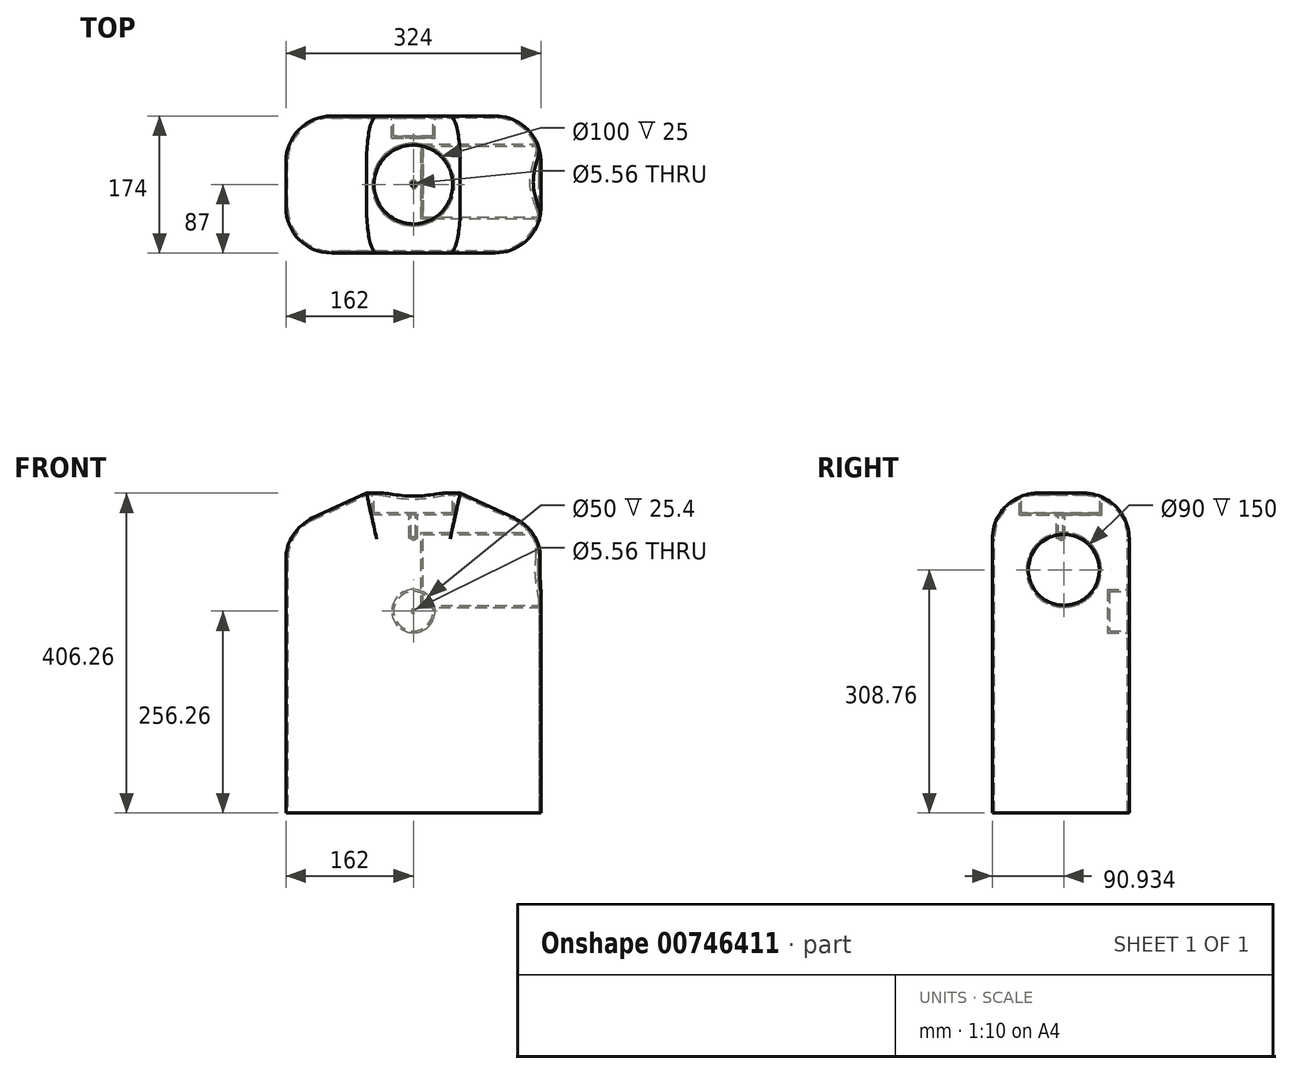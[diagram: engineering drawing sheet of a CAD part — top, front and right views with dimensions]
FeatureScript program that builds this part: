
annotation { "Feature Type Name" : "Feature", "Feature Type Description" : "" }
export const myFeature = defineFeature(function(context is Context, id is Id, definition is map)
    precondition{}
    {
        {
            var Q0;
            Q0=qCreatedBy(makeId("Front.planeOp"),FACE);
            var sketch = newSketch(context, id + "F0", { "sketchPlane" : qUnion([Q0])});
            skLineSegment(sketch, "E0.bottom", {"start": v(162, 203.13) * mm, "end": v(-162, 203.13) * mm});
            skLineSegment(sketch, "E0.top", {"start": v(162, -203.13) * mm, "end": v(-162, -203.13) * mm});
            skLineSegment(sketch, "E0.left", {"start": v(162, 203.13) * mm, "end": v(162, -203.13) * mm});
            skLineSegment(sketch, "E0.right", {"start": v(-162, 203.13) * mm, "end": v(-162, -203.13) * mm});
            skPoint(sketch, "E0.middle", {"position": v(0, 0) * mm});
            skSolve(sketch);
        }
        {
            var Q0;
            Q0=makeQuery(id+"F0.imprint","IMPRINT",FACE,{"disambiguationData":[TD([[makeQuery(id+"F0.imprint","IMPRINT",EDGE,{"derivedFrom":sQuery(id+"F0.wireOp",EDGE,"E0.bottom")}),1.0]])]});
            extrude(context, id + "F1", {"entities" : qUnion([Q0]), "depth" : 174 * mm, "offsetDistance" : 25 * mm});
        }
        {
            var Q0;
            Q0=makeQuery(id+"F1.opExtrude","SWEPT_FACE",FACE,{"disambiguationData":[OSD([sQuery(id+"F0.wireOp",EDGE,"E0.bottom")])]});
            var sketch = newSketch(context, id + "F2", { "sketchPlane" : qUnion([Q0])});
            skCircle(sketch, "E1", {"center": v(0, -87) * mm, "radius": 50 * mm});
            skPoint(sketch, "E1.centerSnap0", {"position": v(-162, -87) * mm});
            skPoint(sketch, "E1.centerSnap1", {"position": v(0, 0) * mm});
            skSolve(sketch);
        }
        {
            var Q0;
            Q0=makeQuery(id+"F2.imprint","IMPRINT",FACE,{"disambiguationData":[TD([[makeQuery(id+"F2.imprint","IMPRINT",EDGE,{"derivedFrom":sQuery(id+"F2.wireOp",EDGE,"E1")}),1.0]])]});
            extrude(context, id + "F3", {"entities" : qUnion([Q0]), "operationType" : NewBodyOperationType.REMOVE, "oppositeDirection" : true, "depth" : 25 * mm, "offsetDistance" : 25 * mm});
        }
        {
            var Q0;
            Q0=makeQuery(id+"F3.boolean.opBoolean","COPY",FACE,{"derivedFrom":makeQuery(id+"F3.opExtrude","CAP_FACE",FACE,{"disambiguationData":[OSD([sQuery(id+"F2.wireOp",EDGE,"E1")])],"isStart":false})});
            var sketch = newSketch(context, id + "F4", { "sketchPlane" : qUnion([Q0])});
            skCircle(sketch, "E2.0.0", {"center": v(0, -87) * mm, "radius": 50 * mm});
            skCircle(sketch, "E3", {"center": v(0, -87) * mm, "radius": 3.17 * mm});
            skSolve(sketch);
        }
        {
            var Q0;
            Q0=sQuery(id+"F4.wireOp",VERTEX,"E2.0.0.center");
            var Q1;
            Q1=makeQuery(id+"F1.opExtrude","SWEPT_BODY",BODY,{"disambiguationData":[OSD([sQuery(id+"F0.wireOp",EDGE,"E0.bottom"),sQuery(id+"F0.wireOp",EDGE,"E0.top"),sQuery(id+"F0.wireOp",EDGE,"E0.left"),sQuery(id+"F0.wireOp",EDGE,"E0.right")])]});
            hole(context, id + "F5", {"style" : HoleStyle.SIMPLE, "endStyle" : HoleEndStyle.BLIND, "standardTappedOrClearance" : lookupTablePath({ "standard" : "ANSI", "engagement" : "50%", "pitch" : "20 tpi", "size" : "1/4", "type" : "Tapped" }), "standardBlindInLast" : lookupTablePath({ "standard" : "ANSI", "engagement" : "50%", "pitch" : "20 tpi", "size" : "1/4", "type" : "Tapped" }), "holeDiameter" : 5.56 * mm, "majorDiameter" : 6.35 * mm, "showTappedDepth" : true, "holeDepth" : 30.48 * mm, "isTappedThrough" : true, "tappedDepth" : 25.4 * mm, "tapClearance" : 4, "locations" : qUnion([Q0]), "scope" : qUnion([Q1])});
        }
        {
            var Q0;
            Q0=makeQuery(id+"F1.opExtrude","SWEPT_EDGE",EDGE,{"disambiguationData":[OSD([sQuery(id+"F0.wireOp",EDGE,"E0.bottom"),sQuery(id+"F0.wireOp",EDGE,"E0.right")])]});
            var Q1;
            Q1=makeQuery(id+"F1.opExtrude","SWEPT_EDGE",EDGE,{"disambiguationData":[OSD([sQuery(id+"F0.wireOp",EDGE,"E0.bottom"),sQuery(id+"F0.wireOp",EDGE,"E0.left")])]});
            chamfer(context, id + "F6", {"entities" : qUnion([Q0, Q1]), "chamferType" : ChamferType.TWO_OFFSETS, "width1" : 47.5 * mm, "oppositeDirection" : false, "width2" : 102.5 * mm, "tangentPropagation" : true});
        }
        {
            var Q0;
            Q0=makeQuery(id+"F6.opChamfer","BLEND_FACE",FACE,{"disambiguationData":[OSD([sQuery(id+"F0.wireOp",EDGE,"E0.bottom"),sQuery(id+"F0.wireOp",EDGE,"E0.left")])]});
            var sketch = newSketch(context, id + "F7", { "sketchPlane" : qUnion([Q0])});
            skLineSegment(sketch, "E4.0.0", {"start": v(-31.42, -174) * mm, "end": v(81.55, -174) * mm});
            skLineSegment(sketch, "E4.0.1", {"start": v(81.55, -174) * mm, "end": v(81.55, 0) * mm});
            skLineSegment(sketch, "E4.0.2", {"start": v(81.55, 0) * mm, "end": v(-31.42, 0) * mm});
            skLineSegment(sketch, "E4.0.3", {"start": v(-31.42, 0) * mm, "end": v(-31.42, -174) * mm});
            skSolve(sketch);
        }
        {
            var Q0;
            {var subQ0=sQuery(id+"F0.wireOp",EDGE,"E0.right");var subQ1=sQuery(id+"F0.wireOp",EDGE,"E0.bottom");Q0=makeQuery(id+"F6.opChamfer","BLEND_EDGE",EDGE,{"blendedFrom":[makeQuery(id+"F1.opExtrude","SWEPT_EDGE",EDGE,{"disambiguationData":[OSD([subQ1,subQ0])]}),makeQuery(id+"F1.opExtrude","CAP_FACE",FACE,{"disambiguationData":[OSD([subQ1,sQuery(id+"F0.wireOp",EDGE,"E0.top"),sQuery(id+"F0.wireOp",EDGE,"E0.left"),subQ0])],"isStart":false})],"blendedInto":[makeQuery(id+"F1.opExtrude","CAP_FACE",FACE,{"disambiguationData":[OSD([subQ1,sQuery(id+"F0.wireOp",EDGE,"E0.top"),sQuery(id+"F0.wireOp",EDGE,"E0.left"),subQ0])],"isStart":false})]});}
            var Q1;
            Q1=makeQuery(id+"F1.opExtrude","CAP_EDGE",EDGE,{"disambiguationData":[OSD([sQuery(id+"F0.wireOp",EDGE,"E0.bottom")])],"isStart":false});
            var Q2;
            {var subQ0=sQuery(id+"F0.wireOp",EDGE,"E0.left");var subQ1=sQuery(id+"F0.wireOp",EDGE,"E0.bottom");Q2=makeQuery(id+"F6.opChamfer","BLEND_EDGE",EDGE,{"blendedFrom":[makeQuery(id+"F1.opExtrude","SWEPT_EDGE",EDGE,{"disambiguationData":[OSD([subQ1,subQ0])]}),makeQuery(id+"F1.opExtrude","CAP_FACE",FACE,{"disambiguationData":[OSD([subQ1,sQuery(id+"F0.wireOp",EDGE,"E0.top"),subQ0,sQuery(id+"F0.wireOp",EDGE,"E0.right")])],"isStart":false})],"blendedInto":[makeQuery(id+"F1.opExtrude","CAP_FACE",FACE,{"disambiguationData":[OSD([subQ1,sQuery(id+"F0.wireOp",EDGE,"E0.top"),subQ0,sQuery(id+"F0.wireOp",EDGE,"E0.right")])],"isStart":false})]});}
            var Q3;
            Q3=makeQuery(id+"F1.opExtrude","CAP_EDGE",EDGE,{"disambiguationData":[OSD([sQuery(id+"F0.wireOp",EDGE,"E0.bottom")])],"isStart":true});
            var Q4;
            {var subQ0=sQuery(id+"F0.wireOp",EDGE,"E0.right");var subQ1=sQuery(id+"F0.wireOp",EDGE,"E0.bottom");Q4=makeQuery(id+"F6.opChamfer","BLEND_EDGE",EDGE,{"blendedFrom":[makeQuery(id+"F1.opExtrude","SWEPT_EDGE",EDGE,{"disambiguationData":[OSD([subQ1,subQ0])]}),makeQuery(id+"F1.opExtrude","CAP_FACE",FACE,{"disambiguationData":[OSD([subQ1,sQuery(id+"F0.wireOp",EDGE,"E0.top"),sQuery(id+"F0.wireOp",EDGE,"E0.left"),subQ0])],"isStart":true})],"blendedInto":[makeQuery(id+"F1.opExtrude","CAP_FACE",FACE,{"disambiguationData":[OSD([subQ1,sQuery(id+"F0.wireOp",EDGE,"E0.top"),sQuery(id+"F0.wireOp",EDGE,"E0.left"),subQ0])],"isStart":true})]});}
            var Q5;
            {var subQ0=sQuery(id+"F0.wireOp",EDGE,"E0.left");var subQ1=sQuery(id+"F0.wireOp",EDGE,"E0.bottom");Q5=makeQuery(id+"F6.opChamfer","BLEND_EDGE",EDGE,{"blendedFrom":[makeQuery(id+"F1.opExtrude","SWEPT_EDGE",EDGE,{"disambiguationData":[OSD([subQ1,subQ0])]}),makeQuery(id+"F1.opExtrude","CAP_FACE",FACE,{"disambiguationData":[OSD([subQ1,sQuery(id+"F0.wireOp",EDGE,"E0.top"),subQ0,sQuery(id+"F0.wireOp",EDGE,"E0.right")])],"isStart":true})],"blendedInto":[makeQuery(id+"F1.opExtrude","CAP_FACE",FACE,{"disambiguationData":[OSD([subQ1,sQuery(id+"F0.wireOp",EDGE,"E0.top"),subQ0,sQuery(id+"F0.wireOp",EDGE,"E0.right")])],"isStart":true})]});}
            var Q6;
            Q6=makeQuery(id+"F1.opExtrude","CAP_EDGE",EDGE,{"disambiguationData":[OSD([sQuery(id+"F0.wireOp",EDGE,"E0.right")])],"isStart":true});
            var Q7;
            Q7=makeQuery(id+"F1.opExtrude","CAP_EDGE",EDGE,{"disambiguationData":[OSD([sQuery(id+"F0.wireOp",EDGE,"E0.right")])],"isStart":false});
            var Q8;
            {var subQ0=sQuery(id+"F0.wireOp",EDGE,"E0.right");Q8=makeQuery(id+"F6.opChamfer","BLEND_EDGE",EDGE,{"blendedFrom":[makeQuery(id+"F1.opExtrude","SWEPT_EDGE",EDGE,{"disambiguationData":[OSD([sQuery(id+"F0.wireOp",EDGE,"E0.bottom"),subQ0])]}),makeQuery(id+"F1.opExtrude","SWEPT_FACE",FACE,{"disambiguationData":[OSD([subQ0])]})],"blendedInto":[makeQuery(id+"F1.opExtrude","SWEPT_FACE",FACE,{"disambiguationData":[OSD([subQ0])]})]});}
            var Q9;
            Q9=makeQuery(id+"F1.opExtrude","CAP_EDGE",EDGE,{"disambiguationData":[OSD([sQuery(id+"F0.wireOp",EDGE,"E0.left")])],"isStart":false});
            var Q10;
            Q10=makeQuery(id+"F1.opExtrude","CAP_EDGE",EDGE,{"disambiguationData":[OSD([sQuery(id+"F0.wireOp",EDGE,"E0.left")])],"isStart":true});
            var Q11;
            {var subQ0=sQuery(id+"F0.wireOp",EDGE,"E0.left");Q11=makeQuery(id+"F6.opChamfer","BLEND_EDGE",EDGE,{"blendedFrom":[makeQuery(id+"F1.opExtrude","SWEPT_EDGE",EDGE,{"disambiguationData":[OSD([sQuery(id+"F0.wireOp",EDGE,"E0.bottom"),subQ0])]}),makeQuery(id+"F1.opExtrude","SWEPT_FACE",FACE,{"disambiguationData":[OSD([subQ0])]})],"blendedInto":[makeQuery(id+"F1.opExtrude","SWEPT_FACE",FACE,{"disambiguationData":[OSD([subQ0])]})]});}
            fillet(context, id + "F8", {"entities" : qUnion([Q0, Q1, Q2, Q3, Q4, Q5, Q6, Q7, Q8, Q9, Q10, Q11]), "radius" : 174 * mm / 3, "tangentPropagation" : true, "allowEdgeOverflow" : false});
        }
        {
            var Q0;
            Q0=makeQuery(id+"F1.opExtrude","SWEPT_FACE",FACE,{"disambiguationData":[OSD([sQuery(id+"F0.wireOp",EDGE,"E0.left")])]});
            var sketch = newSketch(context, id + "F9", { "sketchPlane" : qUnion([Q0])});
            skCircle(sketch, "E5", {"center": v(-83.07, 105.63) * mm, "radius": 45 * mm});
            skSolve(sketch);
        }
        {
            var Q0;
            Q0=makeQuery(id+"F9.imprint","IMPRINT",FACE,{"disambiguationData":[TD([[makeQuery(id+"F9.imprint","IMPRINT",EDGE,{"derivedFrom":sQuery(id+"F9.wireOp",EDGE,"E5")}),1.0]])]});
            extrude(context, id + "F10", {"entities" : qUnion([Q0]), "operationType" : NewBodyOperationType.REMOVE, "oppositeDirection" : true, "depth" : 150 * mm, "offsetDistance" : 25 * mm});
        }
        {
            var Q0;
            Q0=makeQuery(id+"F1.opExtrude","CAP_FACE",FACE,{"disambiguationData":[OSD([sQuery(id+"F0.wireOp",EDGE,"E0.bottom"),sQuery(id+"F0.wireOp",EDGE,"E0.top"),sQuery(id+"F0.wireOp",EDGE,"E0.left"),sQuery(id+"F0.wireOp",EDGE,"E0.right")])],"isStart":true});
            var sketch = newSketch(context, id + "F11", { "sketchPlane" : qUnion([Q0])});
            skCircle(sketch, "E6", {"center": v(0, 53.13) * mm, "radius": 25 * mm});
            skSolve(sketch);
        }
        {
            var Q0;
            Q0=makeQuery(id+"F11.imprint","IMPRINT",FACE,{"disambiguationData":[TD([[makeQuery(id+"F11.imprint","IMPRINT",EDGE,{"derivedFrom":sQuery(id+"F11.wireOp",EDGE,"E6")}),1.0]])]});
            extrude(context, id + "F12", {"entities" : qUnion([Q0]), "operationType" : NewBodyOperationType.REMOVE, "oppositeDirection" : true, "depth" : 25.4 * mm, "offsetDistance" : 25 * mm});
        }
        {
            var Q0;
            Q0=makeQuery(id+"F1.opExtrude","SWEPT_FACE",FACE,{"disambiguationData":[OSD([sQuery(id+"F0.wireOp",EDGE,"E0.top")])]});
            shell(context, id + "F13", {"entities" : qUnion([Q0]), "thickness" : 2.5 * mm});
        }
        {
            var Q0;
            Q0=makeQuery(id+"F12.boolean.opBoolean","COPY",FACE,{"derivedFrom":makeQuery(id+"F12.opExtrude","CAP_FACE",FACE,{"disambiguationData":[OSD([sQuery(id+"F11.wireOp",EDGE,"E6")])],"isStart":false})});
            var sketch = newSketch(context, id + "F14", { "sketchPlane" : qUnion([Q0])});
            skCircle(sketch, "E7.0.0", {"center": v(0, 53.13) * mm, "radius": 25 * mm});
            skCircle(sketch, "E8", {"center": v(0, 53.13) * mm, "radius": 3.18 * mm});
            skSolve(sketch);
        }
        {
            var Q0;
            Q0=sQuery(id+"F14.wireOp",VERTEX,"E7.0.0.center");
            var Q1;
            Q1=makeQuery(id+"F1.opExtrude","SWEPT_BODY",BODY,{"disambiguationData":[OSD([sQuery(id+"F0.wireOp",EDGE,"E0.bottom"),sQuery(id+"F0.wireOp",EDGE,"E0.top"),sQuery(id+"F0.wireOp",EDGE,"E0.left"),sQuery(id+"F0.wireOp",EDGE,"E0.right")])]});
            hole(context, id + "F15", {"style" : HoleStyle.SIMPLE, "endStyle" : HoleEndStyle.BLIND, "standardTappedOrClearance" : lookupTablePath({ "standard" : "ANSI", "engagement" : "50%", "pitch" : "20 tpi", "size" : "1/4", "type" : "Tapped" }), "standardBlindInLast" : lookupTablePath({ "standard" : "ANSI", "engagement" : "50%", "pitch" : "20 tpi", "size" : "1/4", "type" : "Tapped" }), "holeDiameter" : 5.56 * mm, "majorDiameter" : 6.35 * mm, "showTappedDepth" : true, "holeDepth" : 30.48 * mm, "isTappedThrough" : true, "tappedDepth" : 25.4 * mm, "tapClearance" : 4, "locations" : qUnion([Q0]), "scope" : qUnion([Q1])});
        }
    });
